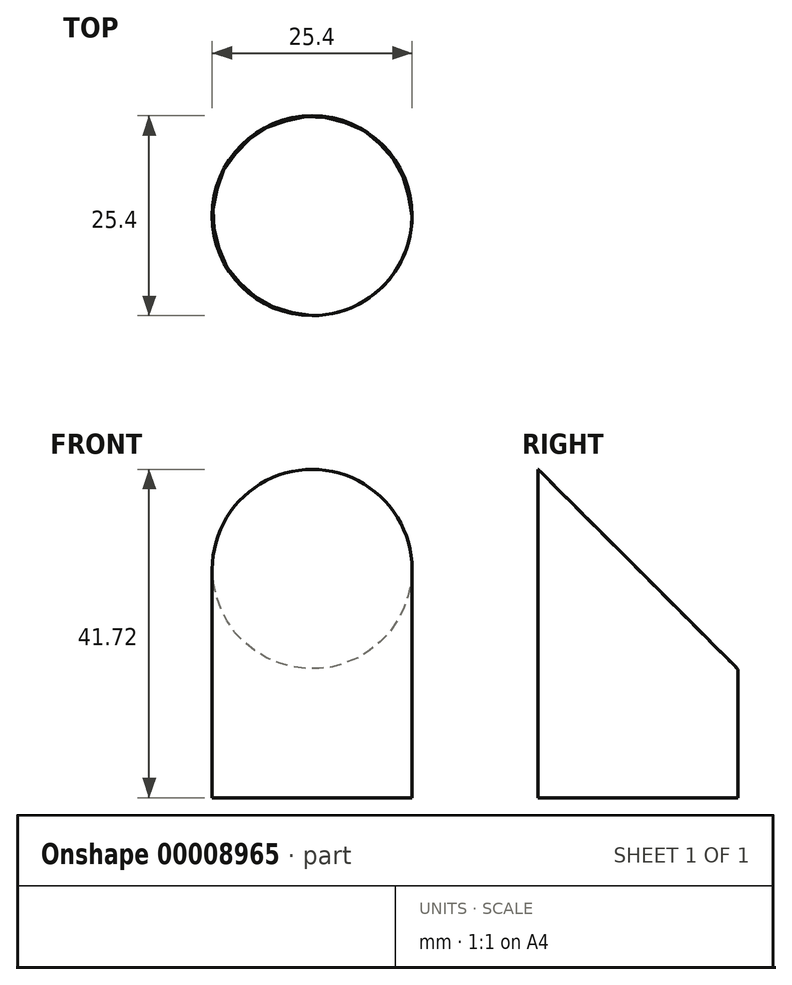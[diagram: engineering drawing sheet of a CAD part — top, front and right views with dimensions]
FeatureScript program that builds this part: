
annotation { "Feature Type Name" : "Feature", "Feature Type Description" : "" }
export const myFeature = defineFeature(function(context is Context, id is Id, definition is map)
    precondition{}
    {
        {
            var Q0;
            Q0=qCreatedBy(makeId("Top.planeOp"),FACE);
            var sketch = newSketch(context, id + "F0", { "sketchPlane" : qUnion([Q0])});
            skLineSegment(sketch, "E0", {"start": v(-52.36, 0) * mm, "end": v(48.2, 0) * mm, "construction": true});
            skCircle(sketch, "E1", {"center": v(-8.73, -29.02) * mm, "radius": 12.7 * mm});
            skSolve(sketch);
        }
        {
            var Q0;
            Q0=sQuery(id+"F0.wireOp",EDGE,"E0");
            cPlane(context, id + "F1", {"entities" : qUnion([Q0]), "cplaneType" : CPlaneType.LINE_ANGLE, "offset" : 152.4 * mm, "angle" : 45 * degree, "width" : 152.4 * mm, "height" : 152.4 * mm});
        }
        {
            var Q0;
            Q0=sQuery(id+"F0.wireOp",EDGE,"E1");
            var Q1;
            Q1=qCreatedBy(id+"F1.planeOp",FACE);
            extrude(context, id + "F2", {"bodyType" : ToolBodyType.SURFACE, "surfaceEntities" : qUnion([Q0]), "endBound" : BoundingType.UP_TO_SURFACE, "endBoundEntityFace" : qUnion([Q1]), "depth" : 25.4 * mm});
        }
    });
